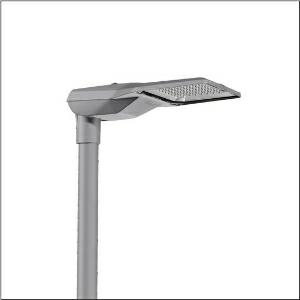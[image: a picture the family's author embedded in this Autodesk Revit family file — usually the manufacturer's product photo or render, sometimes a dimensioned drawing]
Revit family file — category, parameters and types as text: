
# Revit family: streetlight_sl_21_midi___p0_8a_5xe3u33s08mb_2792
name_source: partatom
category: Lighting Fixtures
units: mm (PartAtom-declared; Revit-internal decimal feet)

## family parameters
Cut with Voids When Loaded = No
Host = Face
Light Source = No
Part Type = Normal
Room Calculation Point = No
Round Connector Dimension = Use Diameter
Shared = No

## types (1)
- --- (1 x LED, 18430 lm, 136 W, 3000K)
    Apparent Load = 136 VA
    CIE Flux Codes = 33 69 96 100 100
    Color Rendering = 70
    Color Temperature = 3000K
    Default Elevation = 1800 mm
    Description = Streetlight SL 21 midi, mast luminaire, primary light control with lens, of PMMA, primary optical cover: cover, of toughened safety glass, transparent, light distribution: P0.8a, light emission: direct distribution, primary light characteristic: asymmetric, installation type: post-top, side-entry, LED, High Power LED, rated luminous flux: 18.430lm, luminous efficacy: 136lm/W, light colour: 730, colour temperature: 3000K, control gear: D4i, control: pre-setting: logarithmic dimming characteristic, flexible luminous flux parameterisation, time-dependent luminous flux control, constant luminous flux control, overheat protection, mains connection: 230..240V, AC, 50/60Hz, start of lifetime: 136W, end of service life: 142W, reduction: 61W, luminaire housing, of diecast aluminium, powder-coated, Siteco® metallic grey (DB 702S), corrosivity category C5 mid according to DIN EN ISO 12944, multi-level sealing system, sealing non-destructively replaceable, inclination adjustable: 0°, 5°, 10°, 15°, please order mast flange separately, length: 644mm, width: 335mm, height: 110mm, mast flange for spigot size: 42mm (side-entry): 5XC10008XM4, 60/48mm (side-entry/post-top): 5XC10108XM2, 76/60mm (side-entry/post-top): 5XC10108XM1, mounting height: 4..8m, Smart Interface above, protection rating (complete): IP66, insulation class (complete): insulation class II (safety insulation), certification: CE, ENEC, ENEC+, VDE, impact resistance: IK09, permissible operating ambient temperature for outdoor applications: -40..+50°C, standard-compliant lighting for roads and squares, packaging unit: 1 piece

Light Distribution: P0.8a
    Height = 111 mm
    Lamp = 1 x LED
    Lamp Light Flux = 18430 lm
    Lamp Power = 136 W
    Lamp count = 1
    Length = 644 mm
    Luminous efficacy = 136 lm/W
    Manufacturer = Siteco
    ModVariant = No
    Model = 5XE3U33S08MB
    Number of Poles = 1
    OnlyDefault = Yes
    Power Factor = 1
    Product Name = Streetlight SL 21 midi | P0.8a
    Product group = mast luminaire | pylon top
    ProductGroupID = 6100
    Protection Class = Protection class II
    Protection Degree = IP 66
    RLX_Detail_Level = 1
    RLX_Emergency_Light_Flux = 0 lm
    RLX_Emergency_Type = 0
    RLX_Emergency_Type_DB = No
    RlxData = <blob elided: 90385 chars, md5=514a4157>
    Socket = socket
    Standby Power = 0 W
    System Light Flux = 18429 lm
    System Power = 136 W
    Type Comments = factory setting: luminous flux: 100 % | dim-lin: 254 | 695 mA
    Type Image = l_1004302.jpg
    URL = http://relux.com
    VarID = @adj_069592
    Voltage = 0 V
    Weight = 0.00 kg
    Width = 336 mm

## geometry (parser evidence)
native form markers: Blend x4, Sweep x10
no freeform markers — native parametric forms only
